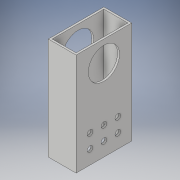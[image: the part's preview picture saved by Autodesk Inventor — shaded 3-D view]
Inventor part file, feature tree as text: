
AUTODESK INVENTOR PART (.ipt)
format: ipt  version: 2018 (Build 220112000, 112)  size: 154,624 bytes
history: native  units: in
note: dims shown in document units (in); Inventor stores cm internally (conversion verified against a paired STEP export)
features: extrude x3, sketch x3
ambient origin geometry x8: Origin, YZ Plane, XZ Plane, XY Plane, X Axis, Y Axis, Z Axis, Center Point
bodies: Solid1 (feature_tree)
feature tree (6):
  extrude  "Extrusion1"  Depth=2.0in
  extrude  "Extrusion2"  Depth=3.675in TaperAngle=0.0deg
  extrude  "Extrusion3"  Depth=1.0in
  sketch  "Sketch2"  dims[d0=1.0in d1=2.0in]
  sketch  "Sketch3"  dims[d2=0.07in d3=3.675in d4=0.0in]
  sketch  "Sketch4"  dims[d5=1.92in d6=1.0in d7=1.125in d8=1.675in d9=0.0in d10=0.5in d11=0.5in d12=0.5in d13=0.5in d14=0.5in d15=0.2031in d16=0.2031in d17=0.5in d25=1.0in d26=0.0in d27=0.5in d28=0.5in d29=0.2031in d30=0.2031in d31=0.5in d32=0.2031in d33=0.2031in]
